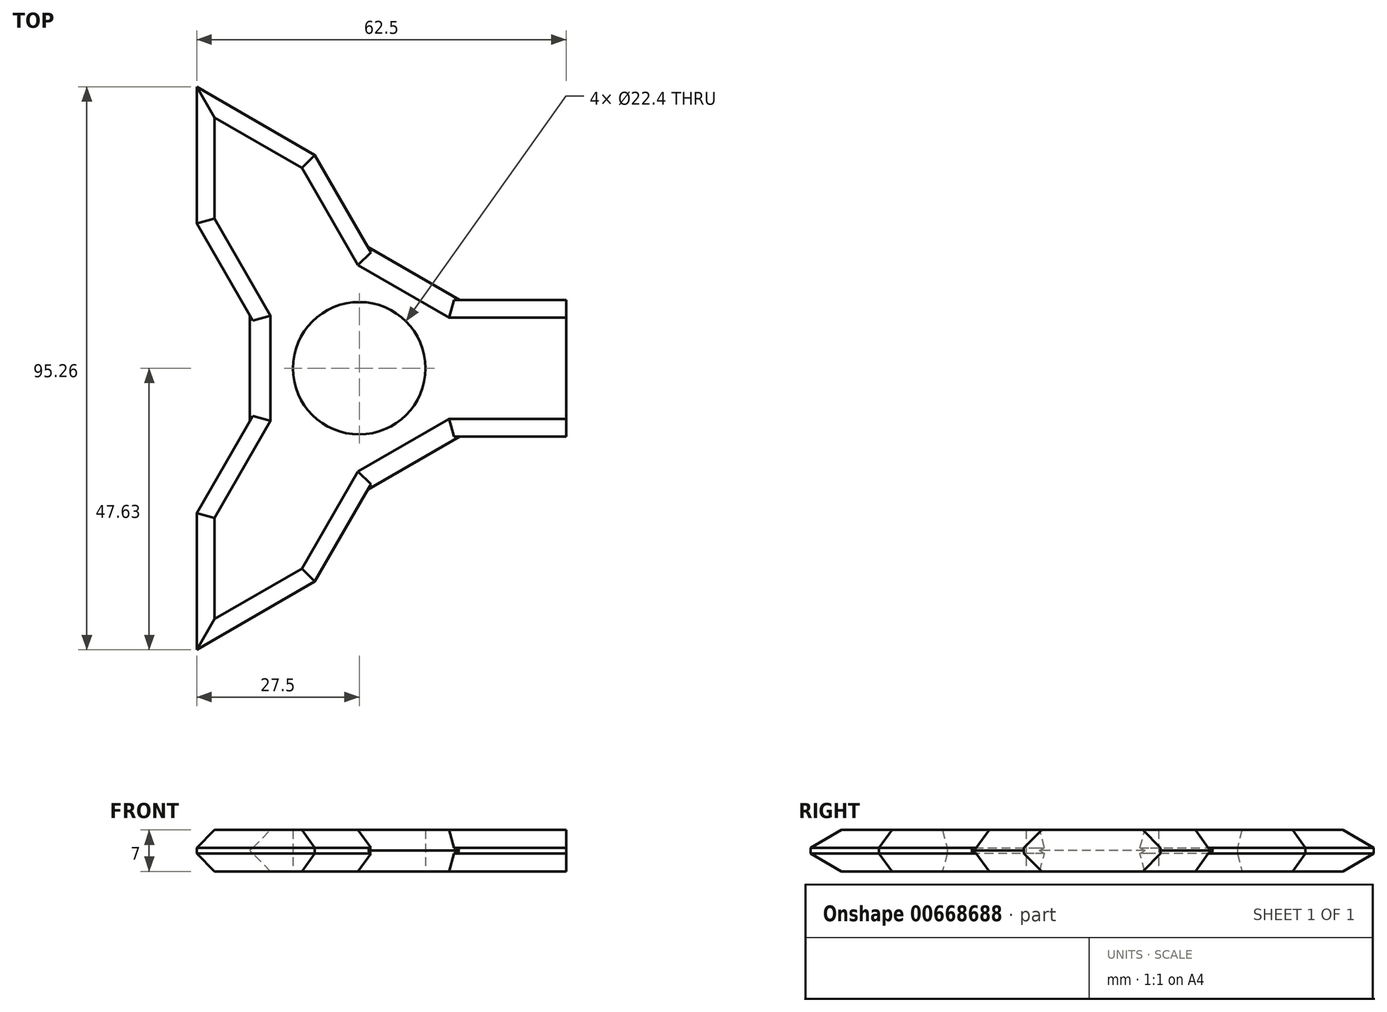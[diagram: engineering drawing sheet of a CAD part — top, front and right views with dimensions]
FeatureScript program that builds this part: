
annotation { "Feature Type Name" : "Feature", "Feature Type Description" : "" }
export const myFeature = defineFeature(function(context is Context, id is Id, definition is map)
    precondition{}
    {
        {
            var Q0;
            Q0=qCreatedBy(makeId("Top.planeOp"),FACE);
            var sketch = newSketch(context, id + "F0", { "sketchPlane" : qUnion([Q0])});
            skCircle(sketch, "E0", {"center": v(0, 0) * mm, "radius": 11.2 * mm});
            skLineSegment(sketch, "E1", {"start": v(0, 0) * mm, "end": v(-20, 0) * mm});
            skLineSegment(sketch, "E2", {"start": v(-20, 0) * mm, "end": v(0, 0) * mm});
            skCircle(sketch, "E3.cCircle", {"center": v(0, 0) * mm, "radius": 20 * mm, "construction": true});
            skLineSegment(sketch, "E3.0", {"start": v(-20, -11.55) * mm, "end": v(-20, 11.55) * mm});
            skLineSegment(sketch, "E3.1", {"start": v(-20, 11.55) * mm, "end": v(0, 23.1) * mm});
            skLineSegment(sketch, "E3.2", {"start": v(0, 23.1) * mm, "end": v(20, 11.55) * mm});
            skLineSegment(sketch, "E3.3", {"start": v(20, 11.55) * mm, "end": v(20, -11.55) * mm});
            skLineSegment(sketch, "E3.4", {"start": v(20, -11.55) * mm, "end": v(0, -23.1) * mm});
            skLineSegment(sketch, "E3.5", {"start": v(0, -23.1) * mm, "end": v(-20, -11.55) * mm});
            skPoint(sketch, "E3.0.midPoint", {"position": v(-20, 0) * mm});
            skLineSegment(sketch, "E4", {"start": v(-20, 11.55) * mm, "end": v(-27.5, 24.54) * mm});
            skLineSegment(sketch, "E5", {"start": v(-27.5, 24.54) * mm, "end": v(0, 23.1) * mm});
            skLineSegment(sketch, "E6", {"start": v(0, 23.1) * mm, "end": v(-7.5, 36.08) * mm});
            skLineSegment(sketch, "E7", {"start": v(-7.5, 36.08) * mm, "end": v(-27.5, 24.54) * mm});
            skLineSegment(sketch, "E8", {"start": v(20, 11.55) * mm, "end": v(35, 11.55) * mm});
            skLineSegment(sketch, "E9", {"start": v(35, 11.55) * mm, "end": v(20, -11.55) * mm});
            skLineSegment(sketch, "E10", {"start": v(20, -11.55) * mm, "end": v(35, -11.55) * mm});
            skLineSegment(sketch, "E11", {"start": v(35, -11.55) * mm, "end": v(35, 11.55) * mm});
            skLineSegment(sketch, "E12", {"start": v(0, -23.1) * mm, "end": v(-7.5, -36.08) * mm});
            skLineSegment(sketch, "E13", {"start": v(-7.5, -36.08) * mm, "end": v(-20, -11.55) * mm});
            skLineSegment(sketch, "E14", {"start": v(-20, -11.55) * mm, "end": v(-27.5, -24.54) * mm});
            skLineSegment(sketch, "E15", {"start": v(-27.5, -24.54) * mm, "end": v(-7.5, -36.08) * mm});
            skLineSegment(sketch, "E16", {"start": v(35, 11.55) * mm, "end": v(35, -11.55) * mm});
            skLineSegment(sketch, "E17", {"start": v(-27.5, 24.54) * mm, "end": v(-17.5, 30.31) * mm});
            skLineSegment(sketch, "E18", {"start": v(-17.5, 30.31) * mm, "end": v(-27.5, 47.63) * mm});
            skLineSegment(sketch, "E19", {"start": v(-27.5, 47.63) * mm, "end": v(-27.5, 24.54) * mm});
            skLineSegment(sketch, "E20", {"start": v(-27.5, 47.63) * mm, "end": v(-7.5, 36.08) * mm});
            skLineSegment(sketch, "E21", {"start": v(35, 11.55) * mm, "end": v(35, 0) * mm});
            skLineSegment(sketch, "E22", {"start": v(35, 0) * mm, "end": v(55, 0) * mm});
            skLineSegment(sketch, "E23", {"start": v(55, 0) * mm, "end": v(35, 11.55) * mm});
            skLineSegment(sketch, "E24", {"start": v(35, -11.55) * mm, "end": v(55, 0) * mm});
            skLineSegment(sketch, "E25", {"start": v(-17.5, -30.31) * mm, "end": v(-27.5, -47.63) * mm});
            skLineSegment(sketch, "E26", {"start": v(-27.5, -47.63) * mm, "end": v(-27.5, -24.54) * mm});
            skLineSegment(sketch, "E27", {"start": v(-27.5, -47.63) * mm, "end": v(-7.5, -36.08) * mm});
            skSolve(sketch);
        }
        {
            var Q0;
            Q0=makeQuery(id+"F0.imprint","IMPRINT",FACE,{"disambiguationData":[TD([[makeQuery(id+"F0.imprint","IMPRINT",EDGE,{"derivedFrom":sQuery(id+"F0.wireOp",EDGE,"E17")}),1.0]])]});
            var Q1;
            Q1=makeQuery(id+"F0.imprint","IMPRINT",FACE,{"disambiguationData":[TD([[makeQuery(id+"F0.imprint","IMPRINT",EDGE,{"derivedFrom":sQuery(id+"F0.wireOp",EDGE,"E7")}),-1.0]])]});
            var Q2;
            Q2=makeQuery(id+"F0.imprint","IMPRINT",FACE,{"disambiguationData":[TD([[makeQuery(id+"F0.imprint","IMPRINT",EDGE,{"derivedFrom":sQuery(id+"F0.wireOp",EDGE,"E5")}),1.0]])]});
            var Q3;
            Q3=makeQuery(id+"F0.imprint","IMPRINT",FACE,{"disambiguationData":[TD([[makeQuery(id+"F0.imprint","IMPRINT",EDGE,{"derivedFrom":sQuery(id+"F0.wireOp",EDGE,"E3.1")}),1.0]])]});
            var Q4;
            Q4=makeQuery(id+"F0.imprint","IMPRINT",FACE,{"disambiguationData":[TD([[makeQuery(id+"F0.imprint","IMPRINT",EDGE,{"derivedFrom":sQuery(id+"F0.wireOp",EDGE,"E0")}),-1.0]])]});
            var Q5;
            Q5=makeQuery(id+"F0.imprint","IMPRINT",FACE,{"disambiguationData":[TD([[makeQuery(id+"F0.imprint","IMPRINT",EDGE,{"derivedFrom":sQuery(id+"F0.wireOp",EDGE,"E3.3")}),1.0]])]});
            var Q6;
            Q6=makeQuery(id+"F0.imprint","IMPRINT",FACE,{"disambiguationData":[TD([[makeQuery(id+"F0.imprint","IMPRINT",EDGE,{"derivedFrom":sQuery(id+"F0.wireOp",EDGE,"E9")}),1.0]])]});
            var Q7;
            Q7=makeQuery(id+"F0.imprint","IMPRINT",FACE,{"disambiguationData":[TD([[makeQuery(id+"F0.imprint","IMPRINT",EDGE,{"derivedFrom":sQuery(id+"F0.wireOp",EDGE,"E21")}),1.0]])]});
            var Q8;
            Q8=makeQuery(id+"F0.imprint","IMPRINT",FACE,{"disambiguationData":[TD([[makeQuery(id+"F0.imprint","IMPRINT",EDGE,{"derivedFrom":sQuery(id+"F0.wireOp",EDGE,"E16")}),1.0]])]});
            var Q9;
            Q9=makeQuery(id+"F0.imprint","IMPRINT",FACE,{"disambiguationData":[TD([[makeQuery(id+"F0.imprint","IMPRINT",EDGE,{"derivedFrom":sQuery(id+"F0.wireOp",EDGE,"E3.5")}),1.0]])]});
            var Q10;
            {var subQ2=sQuery(id+"F0.wireOp",EDGE,"E25");Q10=makeQuery(id+"F0.imprint","IMPRINT",FACE,{"disambiguationData":[TD([[makeQuery(id+"F0.imprint","IMPRINT",EDGE,{"derivedFrom":subQ2}),1.0]])]});}
            var Q11;
            {var subQ2=sQuery(id+"F0.wireOp",EDGE,"E25");Q11=makeQuery(id+"F0.imprint","IMPRINT",FACE,{"disambiguationData":[TD([[makeQuery(id+"F0.imprint","IMPRINT",EDGE,{"derivedFrom":subQ2}),-1.0]])]});}
            var Q12;
            {var subQ0=sQuery(id+"F0.wireOp",EDGE,"E13");Q12=makeQuery(id+"F0.imprint","IMPRINT",FACE,{"disambiguationData":[TD([[makeQuery(id+"F0.imprint","IMPRINT",EDGE,{"derivedFrom":subQ0}),1.0]])]});}
            extrude(context, id + "F1", {"entities" : qUnion([Q0, Q1, Q2, Q3, Q4, Q5, Q6, Q7, Q8, Q9, Q10, Q11, Q12]), "depth" : 7 * mm, "offsetDistance" : 25 * mm});
        }
        {
            var Q0;
            Q0=makeQuery(id+"F1.opExtrude","CAP_EDGE",EDGE,{"disambiguationData":[OSD([sQuery(id+"F0.wireOp",EDGE,"E19")])],"isStart":false});
            var Q1;
            Q1=makeQuery(id+"F1.opExtrude","CAP_EDGE",EDGE,{"disambiguationData":[OSD([sQuery(id+"F0.wireOp",EDGE,"E6")])],"isStart":false});
            var Q2;
            Q2=makeQuery(id+"F1.opExtrude","CAP_EDGE",EDGE,{"disambiguationData":[OSD([sQuery(id+"F0.wireOp",EDGE,"E4")])],"isStart":false});
            var Q3;
            Q3=makeQuery(id+"F1.opExtrude","CAP_EDGE",EDGE,{"disambiguationData":[OSD([sQuery(id+"F0.wireOp",EDGE,"E20")])],"isStart":false});
            var Q4;
            Q4=makeQuery(id+"F1.opExtrude","CAP_EDGE",EDGE,{"disambiguationData":[OSD([sQuery(id+"F0.wireOp",EDGE,"E8")])],"isStart":false});
            var Q5;
            Q5=makeQuery(id+"F1.opExtrude","CAP_EDGE",EDGE,{"disambiguationData":[OSD([sQuery(id+"F0.wireOp",EDGE,"E23")])],"isStart":false});
            var Q6;
            Q6=makeQuery(id+"F1.opExtrude","CAP_EDGE",EDGE,{"disambiguationData":[OSD([sQuery(id+"F0.wireOp",EDGE,"E24")])],"isStart":false});
            var Q7;
            Q7=makeQuery(id+"F1.opExtrude","CAP_EDGE",EDGE,{"disambiguationData":[OSD([sQuery(id+"F0.wireOp",EDGE,"E10")])],"isStart":false});
            var Q8;
            Q8=makeQuery(id+"F1.opExtrude","CAP_EDGE",EDGE,{"disambiguationData":[OSD([sQuery(id+"F0.wireOp",EDGE,"E12")])],"isStart":false});
            var Q9;
            Q9=makeQuery(id+"F1.opExtrude","CAP_EDGE",EDGE,{"disambiguationData":[OSD([sQuery(id+"F0.wireOp",EDGE,"E27")])],"isStart":false});
            var Q10;
            Q10=makeQuery(id+"F1.opExtrude","CAP_EDGE",EDGE,{"disambiguationData":[OSD([sQuery(id+"F0.wireOp",EDGE,"E26")])],"isStart":false});
            var Q11;
            Q11=makeQuery(id+"F1.opExtrude","CAP_EDGE",EDGE,{"disambiguationData":[OSD([sQuery(id+"F0.wireOp",EDGE,"E14")])],"isStart":false});
            var Q12;
            Q12=makeQuery(id+"F1.opExtrude","CAP_EDGE",EDGE,{"disambiguationData":[OSD([sQuery(id+"F0.wireOp",EDGE,"E20")])],"isStart":true});
            var Q13;
            Q13=makeQuery(id+"F1.opExtrude","CAP_EDGE",EDGE,{"disambiguationData":[OSD([sQuery(id+"F0.wireOp",EDGE,"E19")])],"isStart":true});
            var Q14;
            Q14=makeQuery(id+"F1.opExtrude","CAP_EDGE",EDGE,{"disambiguationData":[OSD([sQuery(id+"F0.wireOp",EDGE,"E6")])],"isStart":true});
            var Q15;
            Q15=makeQuery(id+"F1.opExtrude","CAP_EDGE",EDGE,{"disambiguationData":[OSD([sQuery(id+"F0.wireOp",EDGE,"E4")])],"isStart":true});
            var Q16;
            Q16=makeQuery(id+"F1.opExtrude","CAP_EDGE",EDGE,{"disambiguationData":[OSD([sQuery(id+"F0.wireOp",EDGE,"E14")])],"isStart":true});
            var Q17;
            Q17=makeQuery(id+"F1.opExtrude","CAP_EDGE",EDGE,{"disambiguationData":[OSD([sQuery(id+"F0.wireOp",EDGE,"E26")])],"isStart":true});
            var Q18;
            Q18=makeQuery(id+"F1.opExtrude","CAP_EDGE",EDGE,{"disambiguationData":[OSD([sQuery(id+"F0.wireOp",EDGE,"E27")])],"isStart":true});
            var Q19;
            Q19=makeQuery(id+"F1.opExtrude","CAP_EDGE",EDGE,{"disambiguationData":[OSD([sQuery(id+"F0.wireOp",EDGE,"E12")])],"isStart":true});
            var Q20;
            Q20=makeQuery(id+"F1.opExtrude","CAP_EDGE",EDGE,{"disambiguationData":[OSD([sQuery(id+"F0.wireOp",EDGE,"E10")])],"isStart":true});
            var Q21;
            Q21=makeQuery(id+"F1.opExtrude","CAP_EDGE",EDGE,{"disambiguationData":[OSD([sQuery(id+"F0.wireOp",EDGE,"E24")])],"isStart":true});
            var Q22;
            Q22=makeQuery(id+"F1.opExtrude","CAP_EDGE",EDGE,{"disambiguationData":[OSD([sQuery(id+"F0.wireOp",EDGE,"E23")])],"isStart":true});
            var Q23;
            Q23=makeQuery(id+"F1.opExtrude","CAP_EDGE",EDGE,{"disambiguationData":[OSD([sQuery(id+"F0.wireOp",EDGE,"E8")])],"isStart":true});
            chamfer(context, id + "F2", {"entities" : qUnion([Q0, Q1, Q2, Q3, Q4, Q5, Q6, Q7, Q8, Q9, Q10, Q11, Q12, Q13, Q14, Q15, Q16, Q17, Q18, Q19, Q20, Q21, Q22, Q23]), "width" : 3 * mm, "tangentPropagation" : true});
        }
        {
            var Q0;
            Q0=makeQuery(id+"F1.opExtrude","CAP_EDGE",EDGE,{"disambiguationData":[OSD([sQuery(id+"F0.wireOp",EDGE,"E3.2")])],"isStart":true});
            var Q1;
            Q1=makeQuery(id+"F1.opExtrude","CAP_EDGE",EDGE,{"disambiguationData":[OSD([sQuery(id+"F0.wireOp",EDGE,"E3.0")])],"isStart":true});
            var Q2;
            Q2=makeQuery(id+"F1.opExtrude","CAP_EDGE",EDGE,{"disambiguationData":[OSD([sQuery(id+"F0.wireOp",EDGE,"E3.4")])],"isStart":true});
            var Q3;
            Q3=makeQuery(id+"F1.opExtrude","CAP_EDGE",EDGE,{"disambiguationData":[OSD([sQuery(id+"F0.wireOp",EDGE,"E3.0")])],"isStart":false});
            var Q4;
            Q4=makeQuery(id+"F1.opExtrude","CAP_EDGE",EDGE,{"disambiguationData":[OSD([sQuery(id+"F0.wireOp",EDGE,"E3.2")])],"isStart":false});
            var Q5;
            Q5=makeQuery(id+"F1.opExtrude","CAP_EDGE",EDGE,{"disambiguationData":[OSD([sQuery(id+"F0.wireOp",EDGE,"E3.4")])],"isStart":false});
            chamfer(context, id + "F3", {"entities" : qUnion([Q0, Q1, Q2, Q3, Q4, Q5]), "width" : 5 * mm, "tangentPropagation" : true});
        }
    });
